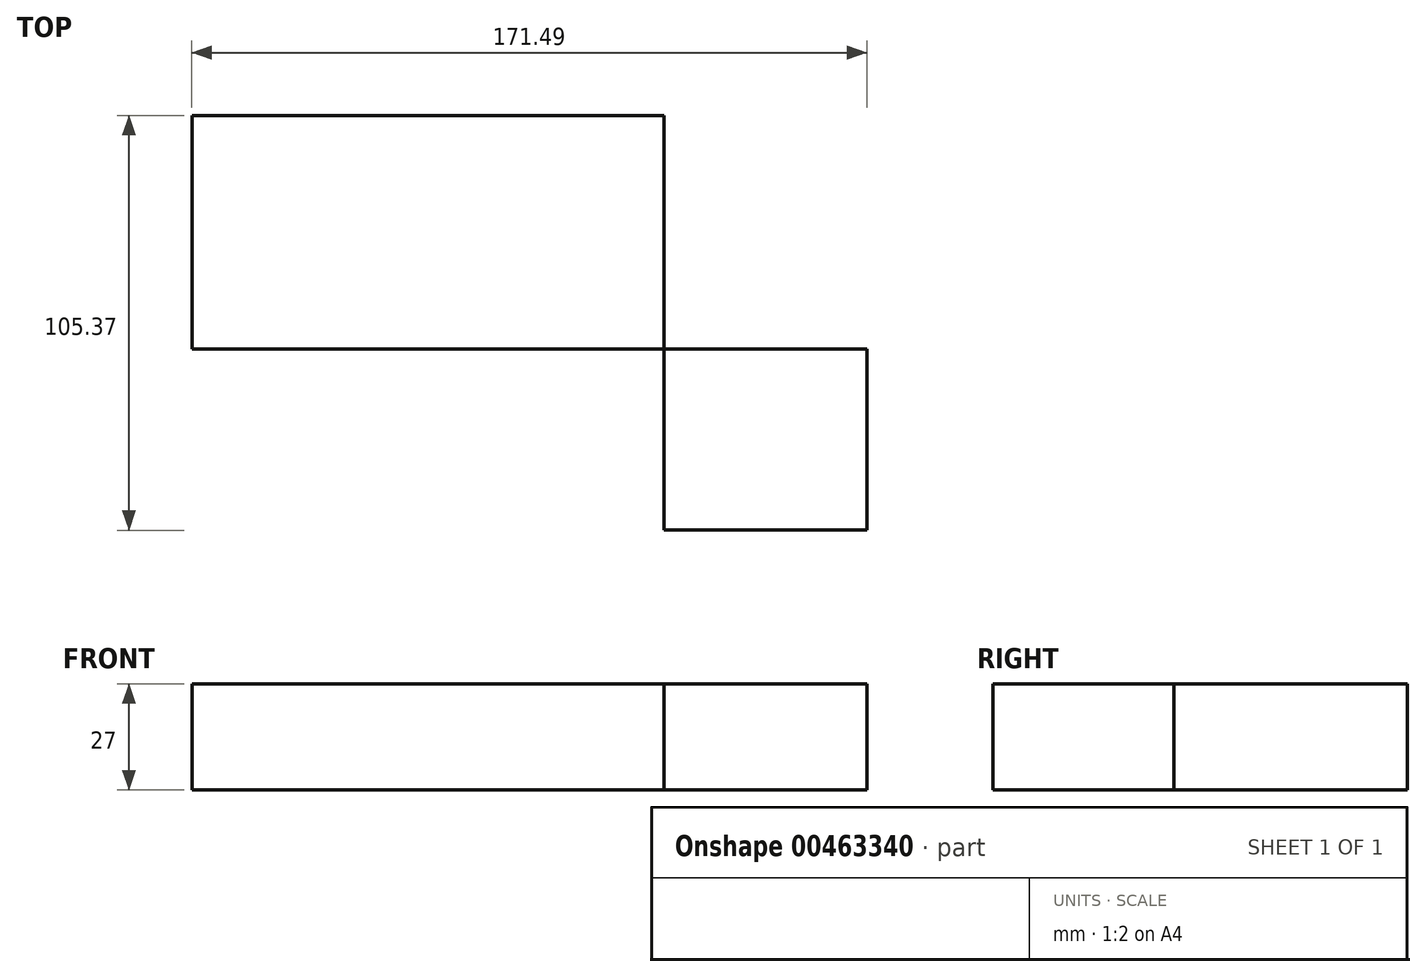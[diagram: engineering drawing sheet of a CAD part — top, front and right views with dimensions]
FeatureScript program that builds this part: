
annotation { "Feature Type Name" : "Feature", "Feature Type Description" : "" }
export const myFeature = defineFeature(function(context is Context, id is Id, definition is map)
    precondition{}
    {
        {
            var Q0;
            Q0=qCreatedBy(makeId("Top.planeOp"),FACE);
            var sketch = newSketch(context, id + "F0", { "sketchPlane" : qUnion([Q0])});
            skLineSegment(sketch, "E0.bottom", {"start": v(-100.27, -24.26) * mm, "end": v(19.62, -24.26) * mm});
            skLineSegment(sketch, "E0.top", {"start": v(-100.27, 35.07) * mm, "end": v(19.62, 35.07) * mm});
            skLineSegment(sketch, "E0.left", {"start": v(-100.27, -24.26) * mm, "end": v(-100.27, 35.07) * mm});
            skLineSegment(sketch, "E0.right", {"start": v(19.62, -24.26) * mm, "end": v(19.62, 35.07) * mm});
            skLineSegment(sketch, "E1.bottom", {"start": v(19.62, -24.26) * mm, "end": v(71.22, -24.26) * mm});
            skLineSegment(sketch, "E1.top", {"start": v(19.62, -70.3) * mm, "end": v(71.22, -70.3) * mm});
            skLineSegment(sketch, "E1.left", {"start": v(19.62, -24.26) * mm, "end": v(19.62, -70.3) * mm});
            skLineSegment(sketch, "E1.right", {"start": v(71.22, -24.26) * mm, "end": v(71.22, -70.3) * mm});
            skSolve(sketch);
        }
        {
            var Q0;
            Q0 = qSketchRegion(id + "F0", true);
            extrude(context, id + "F1", {"entities" : qUnion([Q0]), "depth" : 27 * mm});
        }
    });
